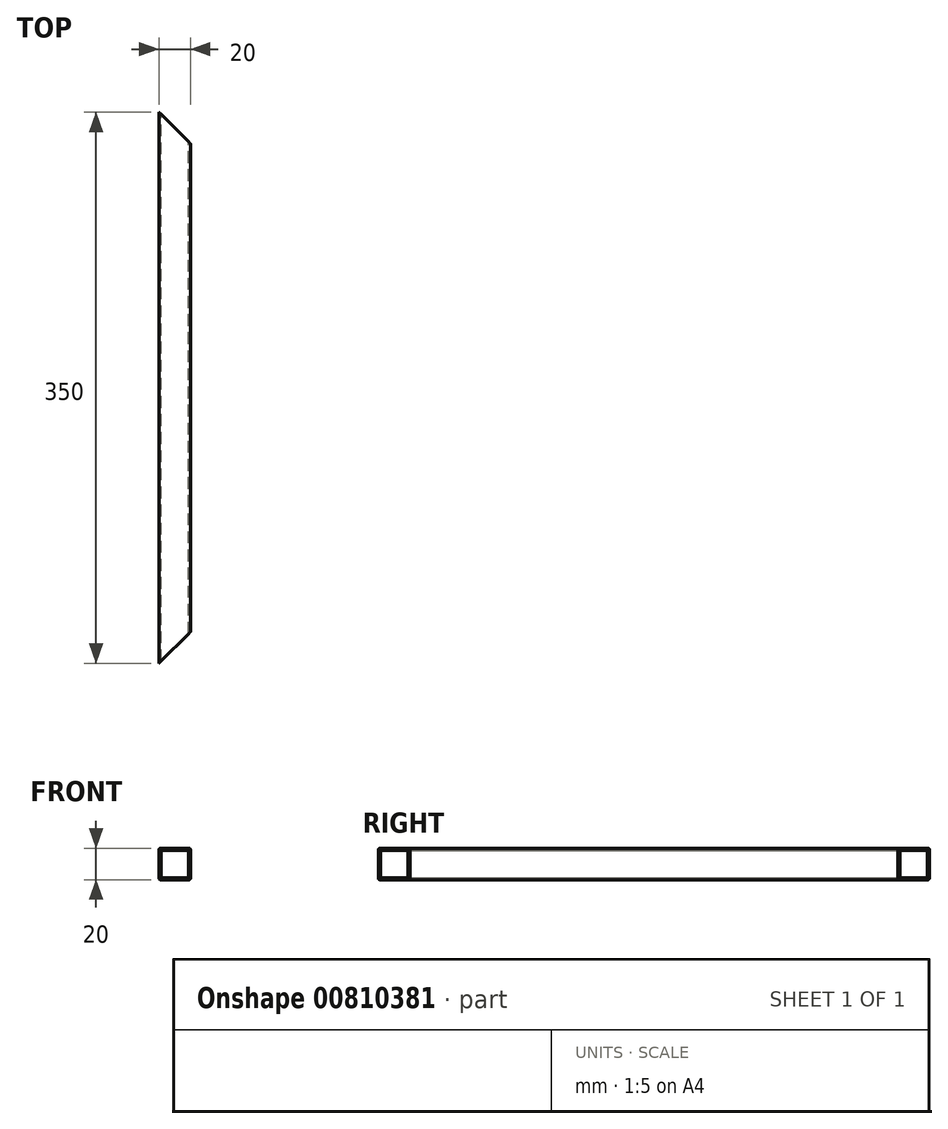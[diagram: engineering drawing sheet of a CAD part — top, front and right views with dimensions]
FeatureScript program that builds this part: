
annotation { "Feature Type Name" : "Feature", "Feature Type Description" : "" }
export const myFeature = defineFeature(function(context is Context, id is Id, definition is map)
    precondition{}
    {
        {
            var Q0;
            Q0=qCreatedBy(makeId("Front.planeOp"),FACE);
            var sketch = newSketch(context, id + "F0", { "sketchPlane" : qUnion([Q0])});
            skLineSegment(sketch, "E0.bottom", {"start": v(-9, 10) * mm, "end": v(9, 10) * mm});
            skLineSegment(sketch, "E0.top", {"start": v(-9, -10) * mm, "end": v(9, -10) * mm});
            skLineSegment(sketch, "E0.left", {"start": v(-10, 9) * mm, "end": v(-10, -9) * mm});
            skLineSegment(sketch, "E0.right", {"start": v(10, 9) * mm, "end": v(10, -9) * mm});
            skPoint(sketch, "E0.middle", {"position": v(0, 0) * mm});
            skLineSegment(sketch, "E1.bottom", {"start": v(-7.75, 8.75) * mm, "end": v(7.75, 8.75) * mm});
            skLineSegment(sketch, "E1.top", {"start": v(-7.75, -8.75) * mm, "end": v(7.75, -8.75) * mm});
            skLineSegment(sketch, "E1.left", {"start": v(-8.75, 7.75) * mm, "end": v(-8.75, -7.75) * mm});
            skLineSegment(sketch, "E1.right", {"start": v(8.75, 7.75) * mm, "end": v(8.75, -7.75) * mm});
            skPoint(sketch, "E2.visualSharp", {"position": v(-10, 10) * mm});
            skArc(sketch, "E2.filletArc", {"start": v(-9, 10) * mm, "mid": v(-9.7, 9.7) * mm, "end": v(-10, 9) * mm});
            skPoint(sketch, "E3.visualSharp", {"position": v(-8.75, 8.75) * mm});
            skArc(sketch, "E3.filletArc", {"start": v(-7.75, 8.75) * mm, "mid": v(-8.46, 8.46) * mm, "end": v(-8.75, 7.75) * mm});
            skPoint(sketch, "E4.visualSharp", {"position": v(8.75, 8.75) * mm});
            skArc(sketch, "E4.filletArc", {"start": v(8.75, 7.75) * mm, "mid": v(8.46, 8.46) * mm, "end": v(7.75, 8.75) * mm});
            skPoint(sketch, "E5.visualSharp", {"position": v(10, 10) * mm});
            skArc(sketch, "E5.filletArc", {"start": v(10, 9) * mm, "mid": v(9.7, 9.7) * mm, "end": v(9, 10) * mm});
            skPoint(sketch, "E6.visualSharp", {"position": v(-10, -10) * mm});
            skArc(sketch, "E6.filletArc", {"start": v(-10, -9) * mm, "mid": v(-9.7, -9.7) * mm, "end": v(-9, -10) * mm});
            skPoint(sketch, "E7.visualSharp", {"position": v(10, -10) * mm});
            skArc(sketch, "E7.filletArc", {"start": v(9, -10) * mm, "mid": v(9.7, -9.7) * mm, "end": v(10, -9) * mm});
            skPoint(sketch, "E8.visualSharp", {"position": v(8.75, -8.75) * mm});
            skArc(sketch, "E8.filletArc", {"start": v(7.75, -8.75) * mm, "mid": v(8.46, -8.46) * mm, "end": v(8.75, -7.75) * mm});
            skPoint(sketch, "E9.visualSharp", {"position": v(-8.75, -8.75) * mm});
            skArc(sketch, "E9.filletArc", {"start": v(-8.75, -7.75) * mm, "mid": v(-8.46, -8.46) * mm, "end": v(-7.75, -8.75) * mm});
            skSolve(sketch);
        }
        {
            var Q0;
            Q0=makeQuery(id+"F0.imprint","IMPRINT",FACE,{"disambiguationData":[TD([[makeQuery(id+"F0.imprint","IMPRINT",EDGE,{"derivedFrom":sQuery(id+"F0.wireOp",EDGE,"E0.bottom")}),-1.0]])]});
            extrude(context, id + "F1", {"entities" : qUnion([Q0]), "depth" : 350 * mm, "offsetDistance" : 25 * mm});
        }
        {
            var Q0;
            Q0=makeQuery(id+"F1.opExtrude","SWEPT_FACE",FACE,{"disambiguationData":[OSD([sQuery(id+"F0.wireOp",EDGE,"E0.bottom")])]});
            var sketch = newSketch(context, id + "F2", { "sketchPlane" : qUnion([Q0])});
            skLineSegment(sketch, "E10", {"start": v(-9, 0) * mm, "end": v(-10, 0) * mm});
            skLineSegment(sketch, "E11", {"start": v(-10, 0) * mm, "end": v(10, -20) * mm});
            skLineSegment(sketch, "E12", {"start": v(10, -20) * mm, "end": v(10, 0) * mm});
            skLineSegment(sketch, "E13", {"start": v(10, 0) * mm, "end": v(-9, 0) * mm});
            skLineSegment(sketch, "E14", {"start": v(9, -175) * mm, "end": v(-9, -175) * mm, "construction": true});
            skLineSegment(sketch, "E15.MirrorCS", {"start": v(-9, -350) * mm, "end": v(-10, -350) * mm});
            skLineSegment(sketch, "E16.MirrorCS", {"start": v(10, -350) * mm, "end": v(-9, -350) * mm});
            skLineSegment(sketch, "E17.MirrorCS", {"start": v(-10, -350) * mm, "end": v(10, -330) * mm});
            skLineSegment(sketch, "E18.MirrorCS", {"start": v(10, -330) * mm, "end": v(10, -350) * mm});
            skSolve(sketch);
        }
        {
            var Q0;
            {var subQ0=sQuery(id+"F2.wireOp",EDGE,"E12");Q0=makeQuery(id+"F2.imprint","IMPRINT",FACE,{"disambiguationData":[TD([[makeQuery(id+"F2.imprint","IMPRINT",EDGE,{"derivedFrom":subQ0}),1.0]])]});}
            var Q1;
            {var subQ0=sQuery(id+"F2.wireOp",EDGE,"E11");var subQ1=sQuery(id+"F0.wireOp",EDGE,"E0.bottom");var subQ2=makeQuery(id+"F1.opExtrude","SWEPT_EDGE",EDGE,{"disambiguationData":[OSD([subQ1,sQuery(id+"F0.wireOp",EDGE,"E2.filletArc")])]});var subQ3=makeQuery(id+"F2.imprint","INTERSECT",VERTEX,{"derivedFrom":[subQ2,subQ0]});Q1=makeQuery(id+"F2.imprint","IMPRINT",FACE,{"disambiguationData":[TD([[makeQuery(id+"F2.imprint","IMPRINT",EDGE,{"disambiguationData":[TD([[subQ3,-1.0]])],"derivedFrom":subQ0}),1.0]])]});}
            var Q2;
            {var subQ1=sQuery(id+"F0.wireOp",EDGE,"E0.bottom");var subQ2=makeQuery(id+"F1.opExtrude","SWEPT_EDGE",EDGE,{"disambiguationData":[OSD([subQ1,sQuery(id+"F0.wireOp",EDGE,"E2.filletArc")])]});var subQ6=sQuery(id+"F2.wireOp",EDGE,"E17.MirrorCS");var subQ8=makeQuery(id+"F2.imprint","INTERSECT",VERTEX,{"derivedFrom":[subQ2,subQ6]});Q2=makeQuery(id+"F2.imprint","IMPRINT",FACE,{"disambiguationData":[TD([[makeQuery(id+"F2.imprint","IMPRINT",EDGE,{"disambiguationData":[TD([[subQ8,-1.0]])],"derivedFrom":subQ6}),-1.0]])]});}
            var Q3;
            {var subQ3=sQuery(id+"F2.wireOp",EDGE,"E18.MirrorCS");Q3=makeQuery(id+"F2.imprint","IMPRINT",FACE,{"disambiguationData":[TD([[makeQuery(id+"F2.imprint","IMPRINT",EDGE,{"derivedFrom":subQ3}),-1.0]])]});}
            var Q4;
            {var subQ0=sQuery(id+"F2.wireOp",EDGE,"E15.MirrorCS");Q4=makeQuery(id+"F2.imprint","IMPRINT",FACE,{"disambiguationData":[TD([[makeQuery(id+"F2.imprint","IMPRINT",EDGE,{"derivedFrom":subQ0}),-1.0]])]});}
            var Q5;
            {var subQ0=sQuery(id+"F2.wireOp",EDGE,"E10");Q5=makeQuery(id+"F2.imprint","IMPRINT",FACE,{"disambiguationData":[TD([[makeQuery(id+"F2.imprint","IMPRINT",EDGE,{"derivedFrom":subQ0}),1.0]])]});}
            extrude(context, id + "F3", {"entities" : qUnion([Q0, Q1, Q2, Q3, Q4, Q5]), "operationType" : NewBodyOperationType.REMOVE, "oppositeDirection" : true, "depth" : 20 * mm, "offsetDistance" : 25 * mm});
        }
    });
